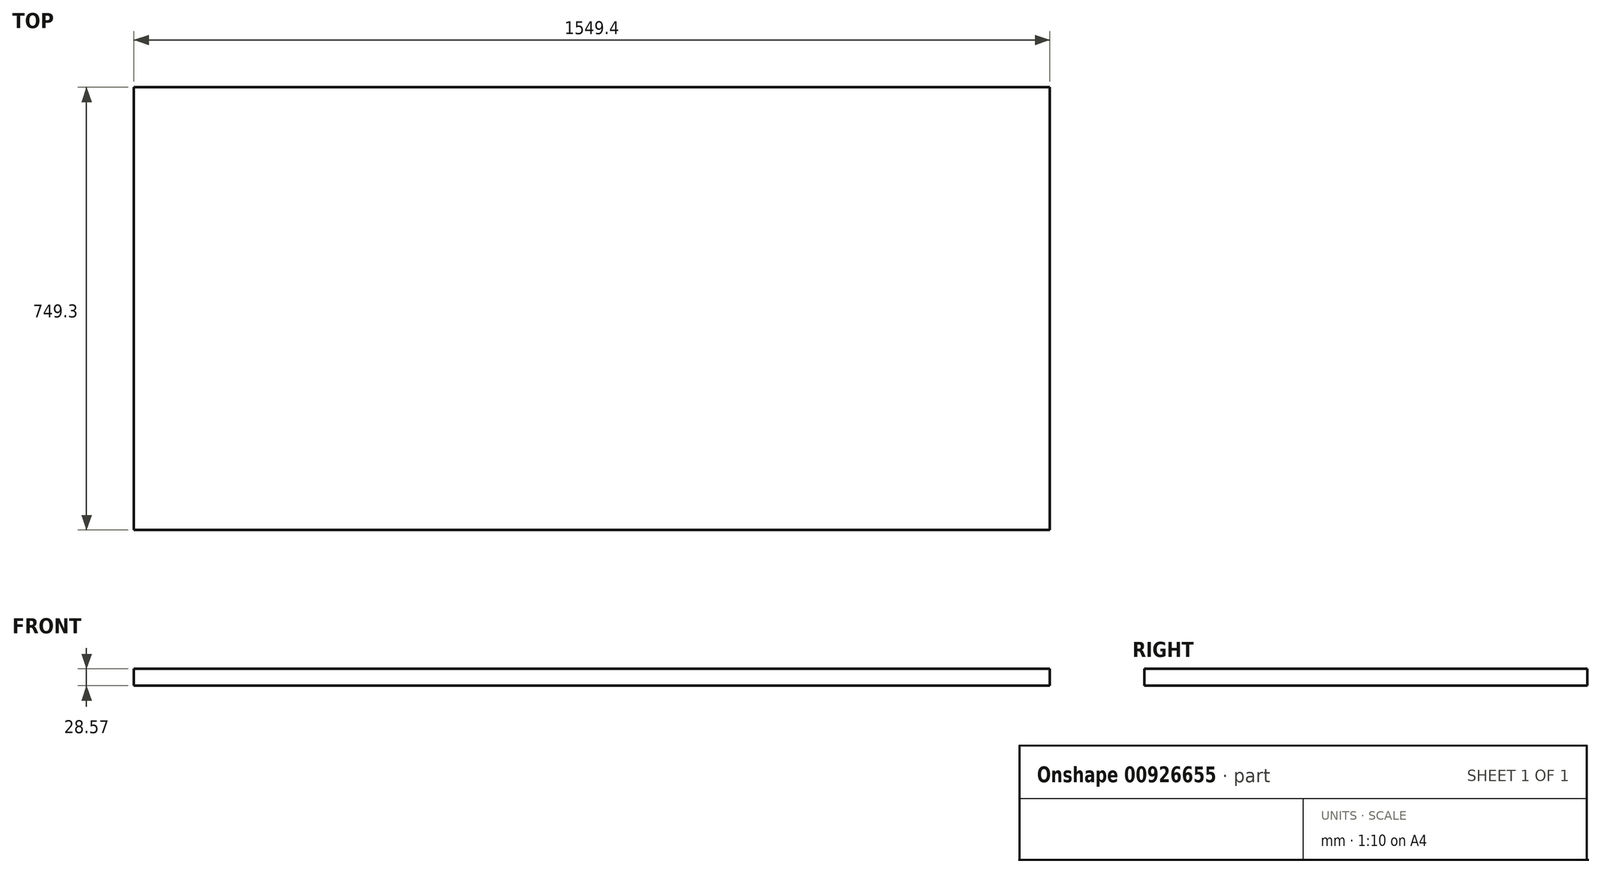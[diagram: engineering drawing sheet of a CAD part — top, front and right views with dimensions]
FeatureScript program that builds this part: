
annotation { "Feature Type Name" : "Feature", "Feature Type Description" : "" }
export const myFeature = defineFeature(function(context is Context, id is Id, definition is map)
    precondition{}
    {
        {
            var Q0;
            Q0=qCreatedBy(makeId("Top.planeOp"),FACE);
            var sketch = newSketch(context, id + "F0", { "sketchPlane" : qUnion([Q0])});
            skLineSegment(sketch, "E0.bottom", {"start": v(-540.43, 375.12) * mm, "end": v(1008.97, 375.12) * mm});
            skLineSegment(sketch, "E0.top", {"start": v(-540.43, -374.18) * mm, "end": v(1008.97, -374.18) * mm});
            skLineSegment(sketch, "E0.left", {"start": v(-540.43, 375.12) * mm, "end": v(-540.43, -374.18) * mm});
            skLineSegment(sketch, "E0.right", {"start": v(1008.97, 375.12) * mm, "end": v(1008.97, -374.18) * mm});
            skSolve(sketch);
        }
        {
            var Q0;
            Q0=makeQuery(id+"F0.imprint","IMPRINT",FACE,{"disambiguationData":[TD([[makeQuery(id+"F0.imprint","IMPRINT",EDGE,{"derivedFrom":sQuery(id+"F0.wireOp",EDGE,"E0.bottom")}),-1.0]])]});
            extrude(context, id + "F1", {"entities" : qUnion([Q0]), "depth" : 28.57 * mm, "offsetDistance" : 25.4 * mm});
        }
    });
